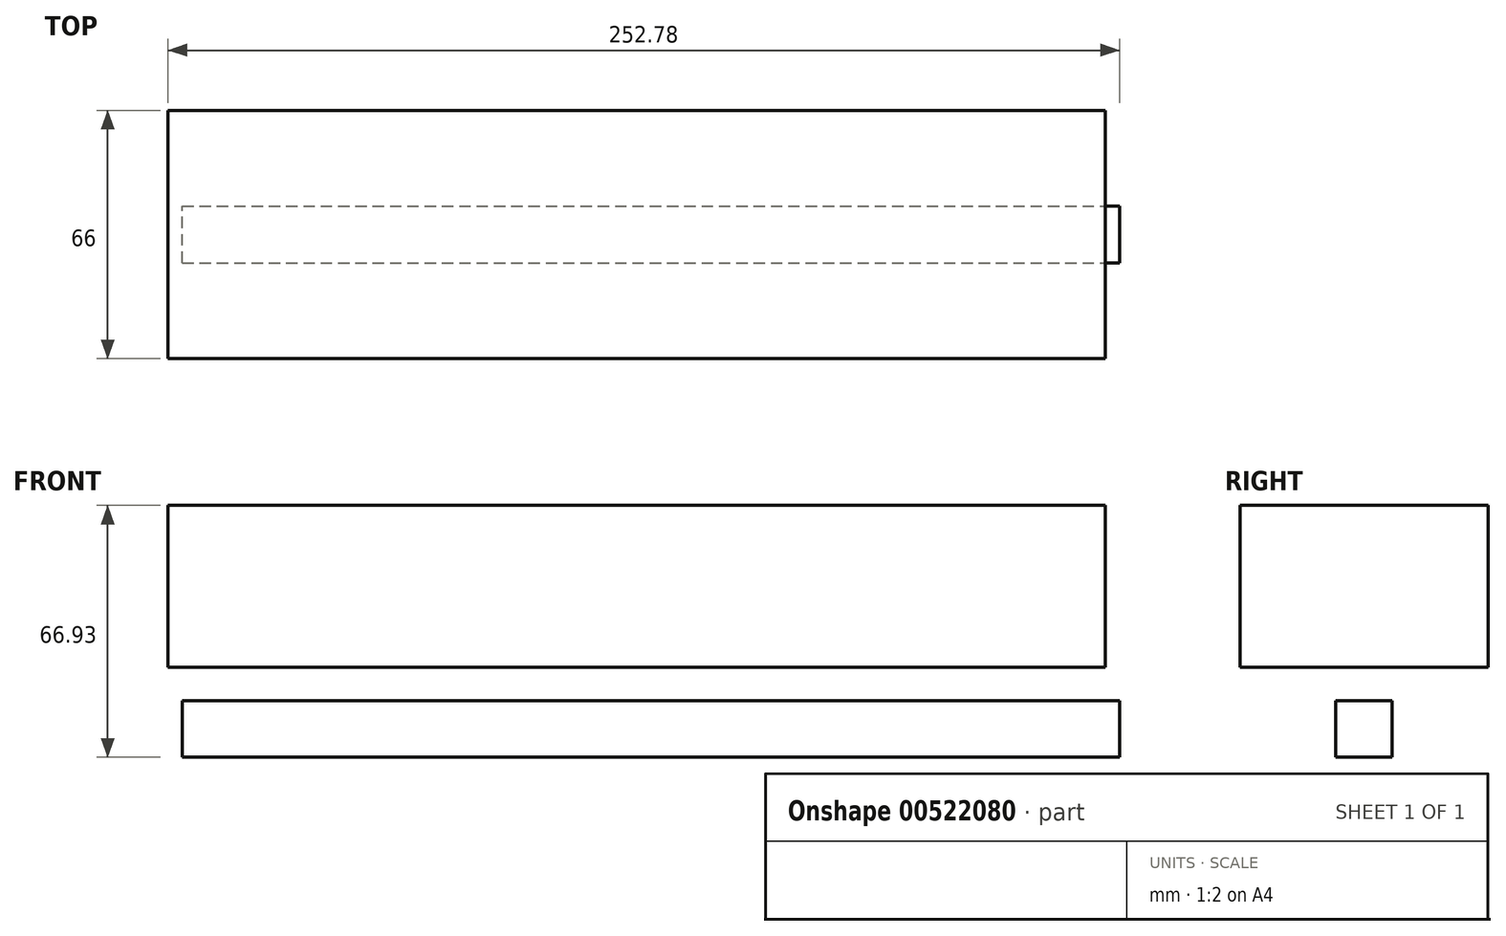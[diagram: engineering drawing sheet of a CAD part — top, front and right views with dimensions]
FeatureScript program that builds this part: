
annotation { "Feature Type Name" : "Feature", "Feature Type Description" : "" }
export const myFeature = defineFeature(function(context is Context, id is Id, definition is map)
    precondition{}
    {
        {
            var Q0;
            Q0=qCreatedBy(makeId("Front.planeOp"),FACE);
            var sketch = newSketch(context, id + "F0", { "sketchPlane" : qUnion([Q0])});
            skLineSegment(sketch, "E0.bottom", {"start": v(-123.35, 15) * mm, "end": v(125.65, 15) * mm});
            skLineSegment(sketch, "E0.top", {"start": v(-123.35, 0) * mm, "end": v(125.65, 0) * mm});
            skLineSegment(sketch, "E0.left", {"start": v(-123.35, 15) * mm, "end": v(-123.35, 0) * mm});
            skLineSegment(sketch, "E0.right", {"start": v(125.65, 15) * mm, "end": v(125.65, 0) * mm});
            skSolve(sketch);
        }
        {
            var Q0;
            Q0=qCreatedBy(makeId("Front.planeOp"),FACE);
            var sketch = newSketch(context, id + "F1", { "sketchPlane" : qUnion([Q0])});
            skLineSegment(sketch, "E1.bottom", {"start": v(-127.13, 66.93) * mm, "end": v(121.87, 66.93) * mm});
            skLineSegment(sketch, "E1.top", {"start": v(-127.13, 23.93) * mm, "end": v(121.87, 23.93) * mm});
            skLineSegment(sketch, "E1.left", {"start": v(-127.13, 66.93) * mm, "end": v(-127.13, 23.93) * mm});
            skLineSegment(sketch, "E1.right", {"start": v(121.87, 66.93) * mm, "end": v(121.87, 23.93) * mm});
            skSolve(sketch);
        }
        {
            var Q0;
            Q0 = qSketchRegion(id + "F1", true);
            extrude(context, id + "F2", {"entities" : qUnion([Q0]), "endBound" : BoundingType.SYMMETRIC, "depth" : 66 * mm, "offsetDistance" : 25 * mm});
        }
        {
            var Q0;
            Q0 = qSketchRegion(id + "F0", true);
            extrude(context, id + "F3", {"entities" : qUnion([Q0]), "operationType" : NewBodyOperationType.ADD, "endBound" : BoundingType.SYMMETRIC, "depth" : 15 * mm, "offsetDistance" : 25 * mm});
        }
    });
